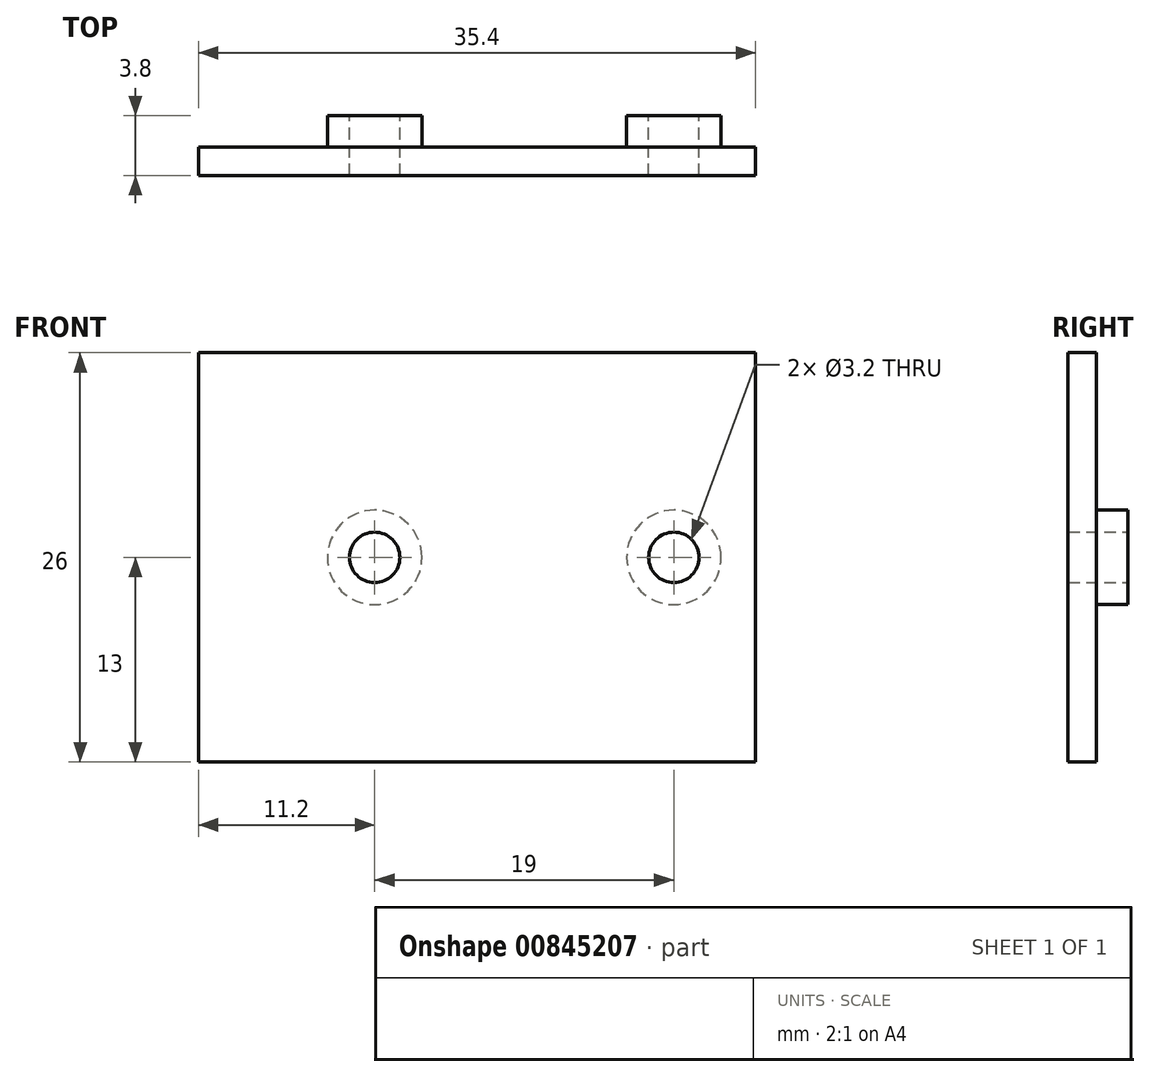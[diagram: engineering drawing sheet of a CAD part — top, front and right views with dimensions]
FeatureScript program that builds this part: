
annotation { "Feature Type Name" : "Feature", "Feature Type Description" : "" }
export const myFeature = defineFeature(function(context is Context, id is Id, definition is map)
    precondition{}
    {
        {
            var Q0;
            Q0=qCreatedBy(makeId("Front.planeOp"),FACE);
            var sketch = newSketch(context, id + "F0", { "sketchPlane" : qUnion([Q0])});
            skLineSegment(sketch, "E0.bottom", {"start": v(-17.7, 13) * mm, "end": v(17.7, 13) * mm});
            skLineSegment(sketch, "E0.top", {"start": v(-17.7, -13) * mm, "end": v(17.7, -13) * mm});
            skLineSegment(sketch, "E0.left", {"start": v(-17.7, 13) * mm, "end": v(-17.7, -13) * mm});
            skLineSegment(sketch, "E0.right", {"start": v(17.7, 13) * mm, "end": v(17.7, -13) * mm});
            skPoint(sketch, "E0.middle", {"position": v(0, 0) * mm});
            skLineSegment(sketch, "E1", {"start": v(-17.7, 0) * mm, "end": v(17.7, 0) * mm, "construction": true});
            skCircle(sketch, "E2", {"center": v(-6.5, 0) * mm, "radius": 1.6 * mm});
            skCircle(sketch, "E3", {"center": v(12.5, 0) * mm, "radius": 1.6 * mm});
            skCircle(sketch, "E4", {"center": v(-6.5, 0) * mm, "radius": 3 * mm});
            skCircle(sketch, "E5", {"center": v(12.5, 0) * mm, "radius": 3 * mm});
            skLineSegment(sketch, "E6.bottom", {"start": v(14.7, 13) * mm, "end": v(-14.7, 13) * mm});
            skLineSegment(sketch, "E6.top", {"start": v(14.7, 11.8) * mm, "end": v(-14.7, 11.8) * mm});
            skLineSegment(sketch, "E6.left", {"start": v(14.7, 13) * mm, "end": v(14.7, 11.8) * mm});
            skLineSegment(sketch, "E6.right", {"start": v(-14.7, 13) * mm, "end": v(-14.7, 11.8) * mm});
            skLineSegment(sketch, "E7.bottom", {"start": v(14.7, -13) * mm, "end": v(-14.7, -13) * mm});
            skLineSegment(sketch, "E7.top", {"start": v(14.7, -11.8) * mm, "end": v(-14.7, -11.8) * mm});
            skLineSegment(sketch, "E7.left", {"start": v(14.7, -13) * mm, "end": v(14.7, -11.8) * mm});
            skLineSegment(sketch, "E7.right", {"start": v(-14.7, -13) * mm, "end": v(-14.7, -11.8) * mm});
            skSolve(sketch);
        }
        {
            var Q0;
            Q0 = qSketchRegion(id + "F0", true);
            var Q1;
            Q1=makeQuery(id+"F0.imprint","IMPRINT",FACE,{"disambiguationData":[TD([[makeQuery(id+"F0.imprint","IMPRINT",EDGE,{"derivedFrom":sQuery(id+"F0.wireOp",EDGE,"BsrFIKC2-SFjy-K68e-kSMu-AN91DG0LeICb")}),-1.0]])]});
            var Q2;
            Q2=makeQuery(id+"F0.imprint","IMPRINT",FACE,{"disambiguationData":[TD([[makeQuery(id+"F0.imprint","IMPRINT",EDGE,{"derivedFrom":sQuery(id+"F0.wireOp",EDGE,"E2")}),-1.0]])]});
            var Q3;
            Q3=makeQuery(id+"F0.imprint","IMPRINT",FACE,{"disambiguationData":[TD([[makeQuery(id+"F0.imprint","IMPRINT",EDGE,{"derivedFrom":sQuery(id+"F0.wireOp",EDGE,"E3")}),-1.0]])]});
            var Q4;
            Q4=makeQuery(id+"F0.imprint","IMPRINT",FACE,{"disambiguationData":[TD([[makeQuery(id+"F0.imprint","IMPRINT",EDGE,{"derivedFrom":sQuery(id+"F0.wireOp",EDGE,"bgwOEZit-ep6a-7gBl-bAeu-S45ZsNgczSUo")}),-1.0]])]});
            extrude(context, id + "F1", {"entities" : qUnion([Q0, Q1, Q2, Q3, Q4]), "depth" : 1.8 * mm, "offsetDistance" : 25 * mm});
        }
        {
            var Q0;
            Q0=makeQuery(id+"F0.imprint","IMPRINT",FACE,{"disambiguationData":[TD([[makeQuery(id+"F0.imprint","IMPRINT",EDGE,{"derivedFrom":sQuery(id+"F0.wireOp",EDGE,"E3")}),-1.0]])]});
            var Q1;
            Q1=makeQuery(id+"F0.imprint","IMPRINT",FACE,{"disambiguationData":[TD([[makeQuery(id+"F0.imprint","IMPRINT",EDGE,{"derivedFrom":sQuery(id+"F0.wireOp",EDGE,"E2")}),-1.0]])]});
            var Q2;
            Q2=makeQuery(id+"F0.imprint","IMPRINT",FACE,{"disambiguationData":[TD([[makeQuery(id+"F0.imprint","IMPRINT",EDGE,{"derivedFrom":sQuery(id+"F0.wireOp",EDGE,"E6.bottom")}),1.0]])]});
            var Q3;
            Q3=makeQuery(id+"F0.imprint","IMPRINT",FACE,{"disambiguationData":[TD([[makeQuery(id+"F0.imprint","IMPRINT",EDGE,{"derivedFrom":sQuery(id+"F0.wireOp",EDGE,"E7.bottom")}),-1.0]])]});
            extrude(context, id + "F2", {"entities" : qUnion([Q0, Q1, Q2, Q3]), "operationType" : NewBodyOperationType.ADD, "oppositeDirection" : true, "depth" : 2 * mm, "offsetDistance" : 25 * mm});
        }
    });
